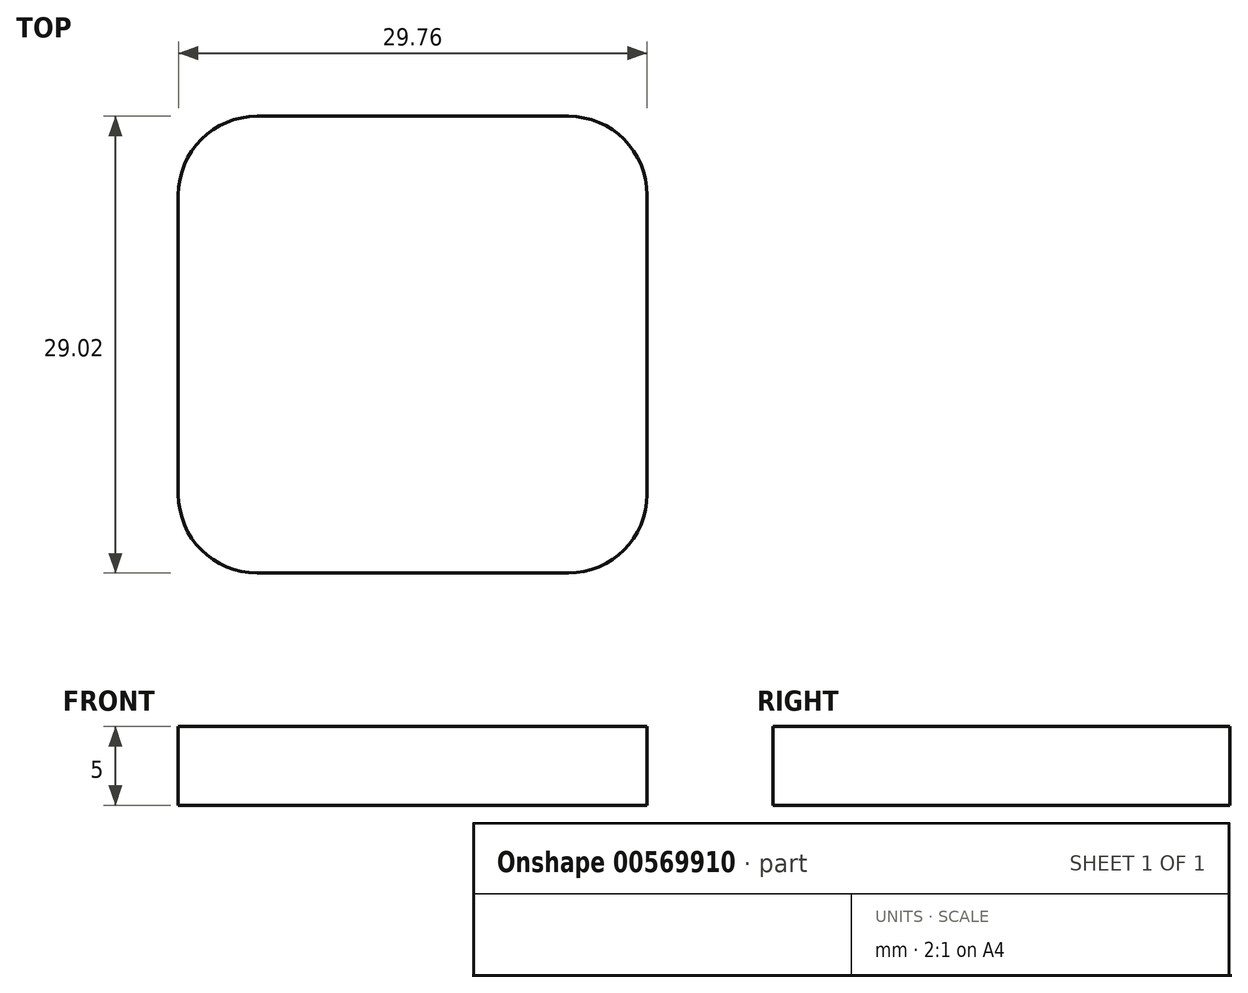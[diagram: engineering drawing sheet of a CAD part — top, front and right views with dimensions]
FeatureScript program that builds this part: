
annotation { "Feature Type Name" : "Feature", "Feature Type Description" : "" }
export const myFeature = defineFeature(function(context is Context, id is Id, definition is map)
    precondition{}
    {
        {
            var Q0;
            Q0=qCreatedBy(makeId("Top.planeOp"),FACE);
            var sketch = newSketch(context, id + "F0", { "sketchPlane" : qUnion([Q0])});
            skLineSegment(sketch, "E0.bottom", {"start": v(14.88, -14.5) * mm, "end": v(-14.88, -14.5) * mm});
            skLineSegment(sketch, "E0.top", {"start": v(14.88, 14.5) * mm, "end": v(-14.88, 14.5) * mm});
            skLineSegment(sketch, "E0.left", {"start": v(14.88, -14.5) * mm, "end": v(14.88, 14.5) * mm});
            skLineSegment(sketch, "E0.right", {"start": v(-14.88, -14.5) * mm, "end": v(-14.88, 14.5) * mm});
            skPoint(sketch, "E0.middle", {"position": v(0, 0) * mm});
            skSolve(sketch);
        }
        {
            var Q0;
            Q0=makeQuery(id+"F0.imprint","IMPRINT",FACE,{"disambiguationData":[TD([[makeQuery(id+"F0.imprint","IMPRINT",EDGE,{"derivedFrom":sQuery(id+"F0.wireOp",EDGE,"E0.bottom")}),-1.0]])]});
            extrude(context, id + "F1", {"entities" : qUnion([Q0]), "depth" : 5 * mm, "offsetDistance" : 25 * mm});
        }
        {
            var Q0;
            Q0=makeQuery(id+"F1.opExtrude","CAP_FACE",FACE,{"disambiguationData":[OSD([sQuery(id+"F0.wireOp",EDGE,"E0.bottom"),sQuery(id+"F0.wireOp",EDGE,"E0.top"),sQuery(id+"F0.wireOp",EDGE,"E0.left"),sQuery(id+"F0.wireOp",EDGE,"E0.right")])],"isStart":false});
            var sketch = newSketch(context, id + "F2", { "sketchPlane" : qUnion([Q0])});
            skCircle(sketch, "E1", {"center": v(0, 0) * mm, "radius": 5 * mm});
            skSolve(sketch);
        }
        {
            var Q0;
            Q0=sQuery(id+"F2.wireOp",EDGE,"E1");
            extrude(context, id + "F3", {"bodyType" : ToolBodyType.SURFACE, "surfaceEntities" : qUnion([Q0]), "depth" : 5 * mm, "offsetDistance" : 25 * mm});
        }
        {
            var Q0;
            Q0=makeQuery(id+"F1.opExtrude","SWEPT_EDGE",EDGE,{"disambiguationData":[OSD([sQuery(id+"F0.wireOp",EDGE,"E0.top"),sQuery(id+"F0.wireOp",EDGE,"E0.left")])]});
            var Q1;
            Q1=makeQuery(id+"F1.opExtrude","SWEPT_EDGE",EDGE,{"disambiguationData":[OSD([sQuery(id+"F0.wireOp",EDGE,"E0.bottom"),sQuery(id+"F0.wireOp",EDGE,"E0.left")])]});
            var Q2;
            Q2=makeQuery(id+"F1.opExtrude","SWEPT_EDGE",EDGE,{"disambiguationData":[OSD([sQuery(id+"F0.wireOp",EDGE,"E0.top"),sQuery(id+"F0.wireOp",EDGE,"E0.right")])]});
            var Q3;
            Q3=makeQuery(id+"F1.opExtrude","SWEPT_EDGE",EDGE,{"disambiguationData":[OSD([sQuery(id+"F0.wireOp",EDGE,"E0.bottom"),sQuery(id+"F0.wireOp",EDGE,"E0.right")])]});
            fillet(context, id + "F4", {"entities" : qUnion([Q0, Q1, Q2, Q3]), "radius" : 5 * mm, "tangentPropagation" : true, "allowEdgeOverflow" : false});
        }
    });
